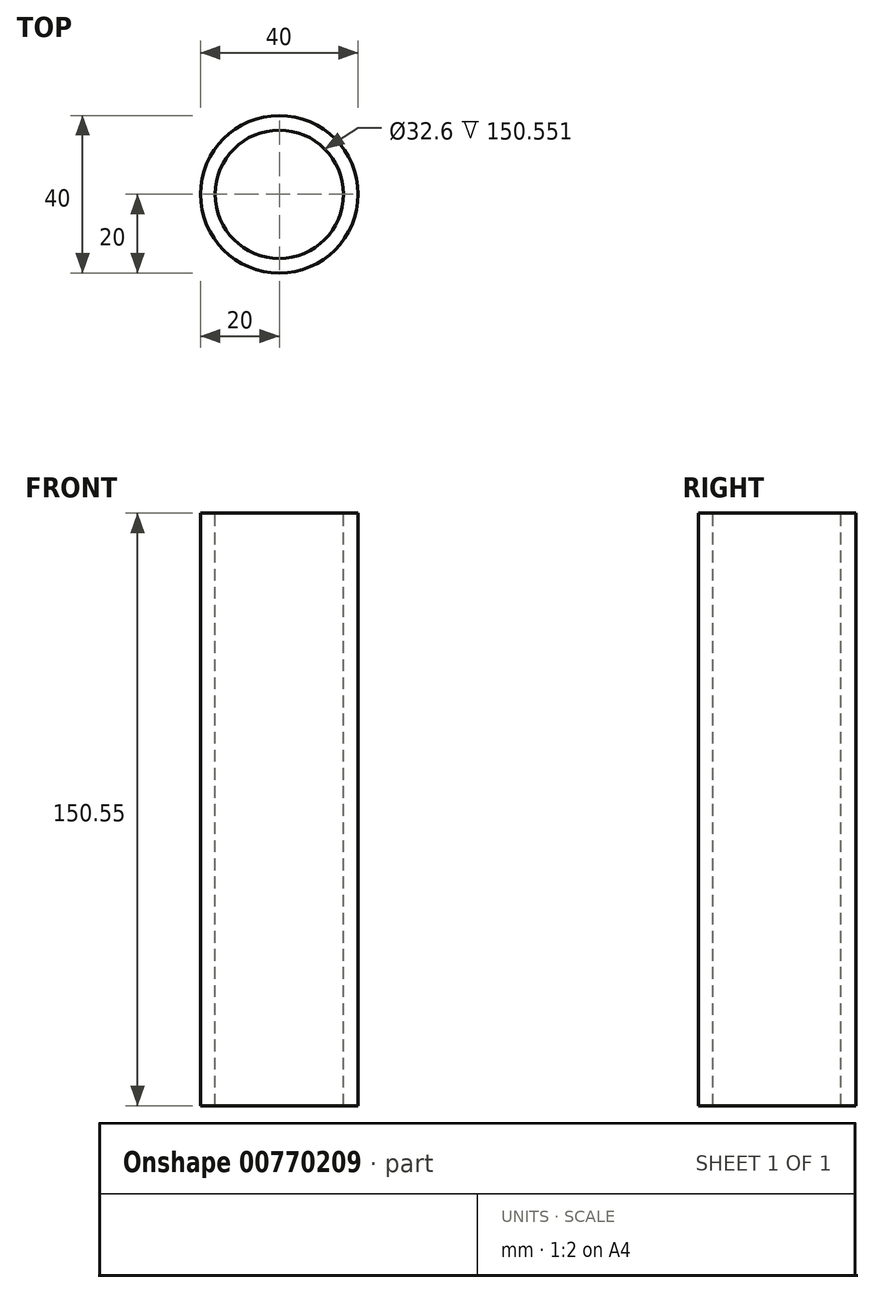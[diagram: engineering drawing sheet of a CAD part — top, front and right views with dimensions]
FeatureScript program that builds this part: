
annotation { "Feature Type Name" : "Feature", "Feature Type Description" : "" }
export const myFeature = defineFeature(function(context is Context, id is Id, definition is map)
    precondition{}
    {
        {
            var Q0;
            Q0=qCreatedBy(makeId("Front.planeOp"),FACE);
            var sketch = newSketch(context, id + "F0", { "sketchPlane" : qUnion([Q0])});
            skLineSegment(sketch, "E0.bottom", {"start": v(0, 70.4) * mm, "end": v(20, 70.4) * mm});
            skLineSegment(sketch, "E0.top", {"start": v(0, -80.16) * mm, "end": v(20, -80.16) * mm});
            skLineSegment(sketch, "E0.left", {"start": v(0, 70.4) * mm, "end": v(0, -80.16) * mm});
            skLineSegment(sketch, "E0.right", {"start": v(20, 70.4) * mm, "end": v(20, -80.16) * mm});
            skSolve(sketch);
        }
        {
            var Q0;
            Q0=makeQuery(id+"F0.imprint","IMPRINT",FACE,{"disambiguationData":[TD([[makeQuery(id+"F0.imprint","IMPRINT",EDGE,{"derivedFrom":sQuery(id+"F0.wireOp",EDGE,"E0.bottom")}),-1.0]])]});
            var Q1;
            Q1=sQuery(id+"F0.wireOp",EDGE,"E0.left");
            revolve(context, id + "F1", {"surfaceOperationType" : NewSurfaceOperationType.NEW, "entities" : qUnion([Q0]), "axis" : qUnion([Q1]), "revolveType" : RevolveType.FULL});
        }
        {
            var Q0;
            Q0=makeQuery(id+"F1.opRevolve","SWEPT_FACE",FACE,{"disambiguationData":[OSD([sQuery(id+"F0.wireOp",EDGE,"E0.top")])]});
            var Q1;
            Q1=makeQuery(id+"F1.opRevolve","SWEPT_FACE",FACE,{"disambiguationData":[OSD([sQuery(id+"F0.wireOp",EDGE,"E0.bottom")])]});
            shell(context, id + "F2", {"entities" : qUnion([Q0, Q1]), "thickness" : 3.7 * mm});
        }
    });
